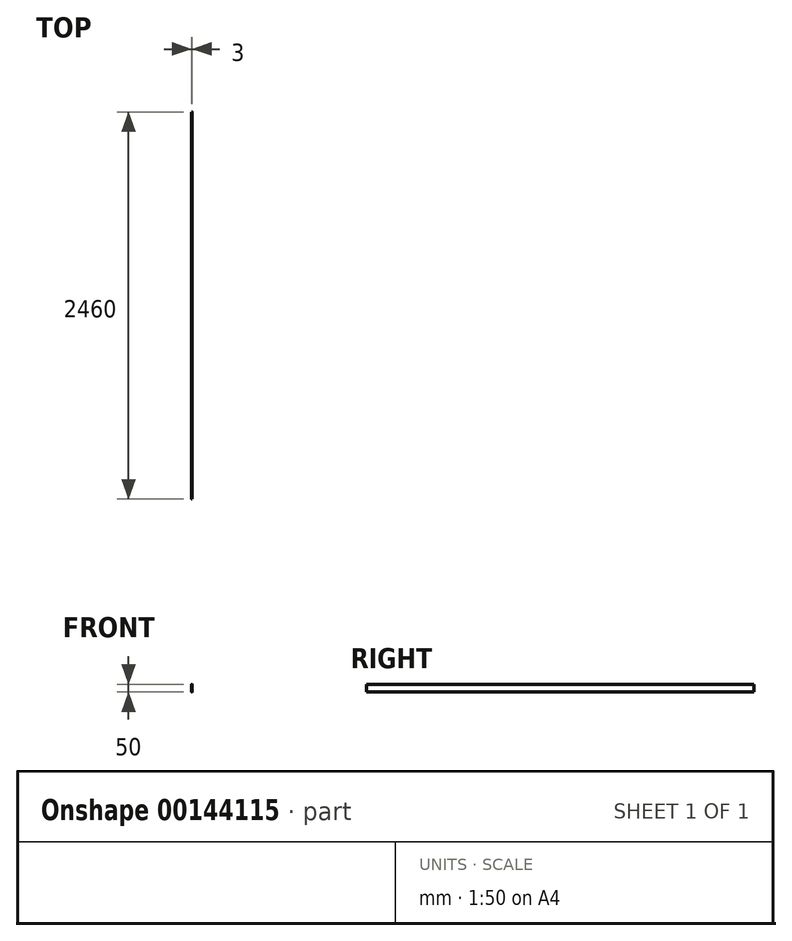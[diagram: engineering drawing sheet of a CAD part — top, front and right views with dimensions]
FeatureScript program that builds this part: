
annotation { "Feature Type Name" : "Feature", "Feature Type Description" : "" }
export const myFeature = defineFeature(function(context is Context, id is Id, definition is map)
    precondition{}
    {
        {
            var Q0;
            Q0=qCreatedBy(makeId("Front.planeOp"),FACE);
            var sketch = newSketch(context, id + "F0", { "sketchPlane" : qUnion([Q0])});
            skLineSegment(sketch, "E0.bottom", {"start": v(1.5, 25) * mm, "end": v(-1.5, 25) * mm});
            skLineSegment(sketch, "E0.top", {"start": v(1.5, -25) * mm, "end": v(-1.5, -25) * mm});
            skLineSegment(sketch, "E0.left", {"start": v(1.5, 25) * mm, "end": v(1.5, -25) * mm});
            skLineSegment(sketch, "E0.right", {"start": v(-1.5, 25) * mm, "end": v(-1.5, -25) * mm});
            skPoint(sketch, "E0.middle", {"position": v(0, 0) * mm});
            skSolve(sketch);
        }
        {
            var Q0;
            Q0 = qSketchRegion(id + "F0", true);
            extrude(context, id + "F1", {"entities" : qUnion([Q0]), "depth" : 2460 * mm});
        }
        {
            var Q0;
            Q0=makeQuery(id+"F1.opExtrude","SWEPT_EDGE",EDGE,{"disambiguationData":[OSD([sQuery(id+"F0.wireOp",EDGE,"E0.bottom"),sQuery(id+"F0.wireOp",EDGE,"E0.left")])]});
            var Q1;
            Q1=makeQuery(id+"F1.opExtrude","SWEPT_EDGE",EDGE,{"disambiguationData":[OSD([sQuery(id+"F0.wireOp",EDGE,"E0.bottom"),sQuery(id+"F0.wireOp",EDGE,"E0.right")])]});
            var Q2;
            Q2=makeQuery(id+"F1.opExtrude","SWEPT_EDGE",EDGE,{"disambiguationData":[OSD([sQuery(id+"F0.wireOp",EDGE,"E0.top"),sQuery(id+"F0.wireOp",EDGE,"E0.left")])]});
            var Q3;
            Q3=makeQuery(id+"F1.opExtrude","SWEPT_EDGE",EDGE,{"disambiguationData":[OSD([sQuery(id+"F0.wireOp",EDGE,"E0.top"),sQuery(id+"F0.wireOp",EDGE,"E0.right")])]});
            fillet(context, id + "F2", {"entities" : qUnion([Q0, Q1, Q2, Q3]), "radius" : 1 * mm, "tangentPropagation" : true, "allowEdgeOverflow" : false});
        }
    });
